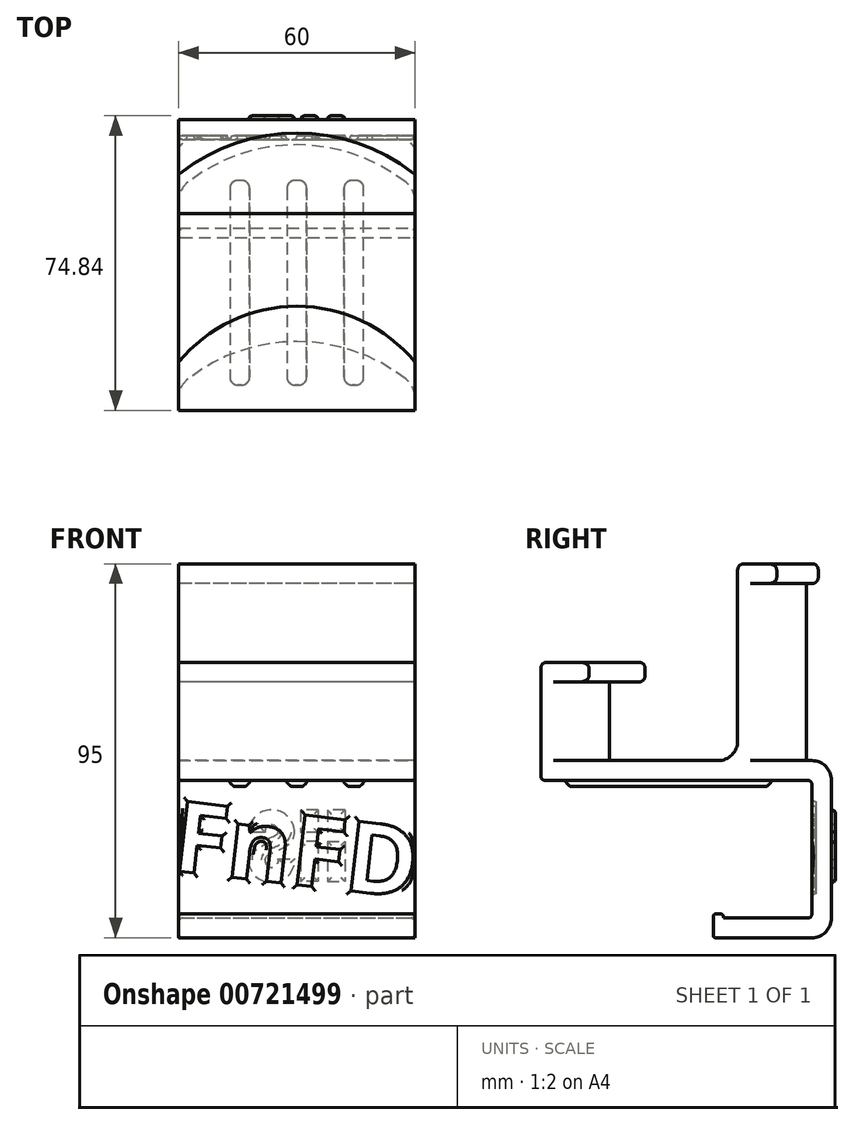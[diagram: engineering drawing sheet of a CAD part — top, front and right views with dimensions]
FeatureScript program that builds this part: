
annotation { "Feature Type Name" : "Feature", "Feature Type Description" : "" }
export const myFeature = defineFeature(function(context is Context, id is Id, definition is map)
    precondition{}
    {
        {
            var Q0;
            Q0=qCreatedBy(makeId("Top.planeOp"),FACE);
            var sketch = newSketch(context, id + "F0", { "sketchPlane" : qUnion([Q0])});
            skArc(sketch, "E0", {"start": v(27.7, 1.93) * mm, "mid": v(0, 11.46) * mm, "end": v(-27.7, 1.93) * mm});
            skLineSegment(sketch, "E1", {"start": v(0, 0) * mm, "end": v(0, -33.54) * mm, "construction": true});
            skLineSegment(sketch, "E2.bottom", {"start": v(-30, 0) * mm, "end": v(30, 0) * mm, "construction": true});
            skLineSegment(sketch, "E2.top", {"start": v(-30, -6) * mm, "end": v(30, -6) * mm});
            skLineSegment(sketch, "E2.left", {"start": v(-30, -2.8) * mm, "end": v(-30, -6) * mm});
            skLineSegment(sketch, "E2.right", {"start": v(30, -2.8) * mm, "end": v(30, -6) * mm});
            skPoint(sketch, "E3.visualSharp", {"position": v(30, 0) * mm});
            skArc(sketch, "E3.filletArc", {"start": v(30, -2.8) * mm, "mid": v(29.4, -0.17) * mm, "end": v(27.7, 1.93) * mm});
            skPoint(sketch, "E4.visualSharp", {"position": v(-30, 0) * mm});
            skArc(sketch, "E4.filletArc", {"start": v(-27.7, 1.93) * mm, "mid": v(-29.4, -0.17) * mm, "end": v(-30, -2.8) * mm});
            skSolve(sketch);
        }
        {
            var Q0;
            Q0=makeQuery(id+"F0.imprint","IMPRINT",FACE,{"disambiguationData":[TD([[makeQuery(id+"F0.imprint","IMPRINT",EDGE,{"derivedFrom":sQuery(id+"F0.wireOp",EDGE,"E0")}),1.0]])]});
            extrude(context, id + "F1", {"entities" : qUnion([Q0]), "depth" : 45 * mm, "offsetDistance" : 25 * mm});
        }
        {
            var Q0;
            Q0=makeQuery(id+"F1.opExtrude","CAP_FACE",FACE,{"disambiguationData":[OSD([sQuery(id+"F0.wireOp",EDGE,"E0"),sQuery(id+"F0.wireOp",EDGE,"E2.top"),sQuery(id+"F0.wireOp",EDGE,"E2.left"),sQuery(id+"F0.wireOp",EDGE,"E2.right"),sQuery(id+"F0.wireOp",EDGE,"E3.filletArc"),sQuery(id+"F0.wireOp",EDGE,"E4.filletArc")])],"isStart":false});
            var sketch = newSketch(context, id + "F2", { "sketchPlane" : qUnion([Q0])});
            skArc(sketch, "E5.0", {"start": v(33, -2.8) * mm, "mid": v(32.09, 1.15) * mm, "end": v(29.54, 4.3) * mm});
            skArc(sketch, "E5.1", {"start": v(-29.54, 4.3) * mm, "mid": v(-32.09, 1.15) * mm, "end": v(-33, -2.8) * mm});
            skLineSegment(sketch, "E5.2", {"start": v(-33, -2.8) * mm, "end": v(-33, -9) * mm});
            skArc(sketch, "E5.3", {"start": v(29.54, 4.3) * mm, "mid": v(0, 14.46) * mm, "end": v(-29.54, 4.3) * mm});
            skLineSegment(sketch, "E5.4", {"start": v(-33, -9) * mm, "end": v(33, -9) * mm});
            skLineSegment(sketch, "E5.5", {"start": v(33, -2.8) * mm, "end": v(33, -9) * mm});
            skLineSegment(sketch, "E6", {"start": v(-30, -6) * mm, "end": v(-33, -6) * mm});
            skPoint(sketch, "E6.endSnap0", {"position": v(-33, -5.9) * mm});
            skLineSegment(sketch, "E7", {"start": v(30, -6) * mm, "end": v(33, -6) * mm});
            skPoint(sketch, "E7.endSnap0", {"position": v(33, -5.9) * mm});
            skSolve(sketch);
        }
        {
            var Q0;
            Q0=makeQuery(id+"F2.imprint","IMPRINT",FACE,{"disambiguationData":[TD([[makeQuery(id+"F2.imprint","IMPRINT",EDGE,{"derivedFrom":sQuery(id+"F2.wireOp",EDGE,"E5.0")}),1.0]])]});
            var Q1;
            Q1=makeQuery(id+"F2.imprint","IMPRINT",FACE,{"disambiguationData":[TD([[makeQuery(id+"F2.imprint","IMPRINT",EDGE,{"derivedFrom":makeQuery(id+"F1.opExtrude","CAP_EDGE",EDGE,{"disambiguationData":[OSD([sQuery(id+"F0.wireOp",EDGE,"E0")])],"isStart":false})}),1.0]])]});
            extrude(context, id + "F3", {"entities" : qUnion([Q0, Q1]), "operationType" : NewBodyOperationType.ADD, "depth" : 5 * mm, "offsetDistance" : 25 * mm});
        }
        {
            var Q0;
            Q0=makeQuery(id+"F1.opExtrude","CAP_EDGE",EDGE,{"disambiguationData":[OSD([sQuery(id+"F0.wireOp",EDGE,"E0")])],"isStart":false});
            var Q1;
            Q1=makeQuery(id+"F3.opExtrude","CAP_EDGE",EDGE,{"disambiguationData":[OSD([sQuery(id+"F2.wireOp",EDGE,"E5.3")])],"isStart":true});
            var Q2;
            Q2=makeQuery(id+"F3.opExtrude","CAP_EDGE",EDGE,{"disambiguationData":[OSD([sQuery(id+"F2.wireOp",EDGE,"E5.3")])],"isStart":false});
            var Q3;
            Q3=makeQuery(id+"F1.opExtrude","CAP_EDGE",EDGE,{"disambiguationData":[OSD([sQuery(id+"F0.wireOp",EDGE,"E4.filletArc")])],"isStart":false});
            var Q4;
            Q4=makeQuery(id+"F3.opExtrude","CAP_EDGE",EDGE,{"disambiguationData":[OSD([sQuery(id+"F2.wireOp",EDGE,"E5.1")])],"isStart":true});
            var Q5;
            Q5=makeQuery(id+"F1.opExtrude","CAP_EDGE",EDGE,{"disambiguationData":[OSD([sQuery(id+"F0.wireOp",EDGE,"E2.left")])],"isStart":false});
            var Q6;
            Q6=makeQuery(id+"F3.opExtrude","CAP_EDGE",EDGE,{"disambiguationData":[OSD([sQuery(id+"F2.wireOp",EDGE,"E5.2")])],"isStart":true});
            var Q7;
            Q7=makeQuery(id+"F3.opExtrude","CAP_EDGE",EDGE,{"disambiguationData":[OSD([sQuery(id+"F2.wireOp",EDGE,"E5.1")])],"isStart":false});
            var Q8;
            Q8=makeQuery(id+"F3.opExtrude","CAP_EDGE",EDGE,{"disambiguationData":[OSD([sQuery(id+"F2.wireOp",EDGE,"E5.2")])],"isStart":false});
            var Q9;
            Q9=makeQuery(id+"F3.opExtrude","CAP_EDGE",EDGE,{"disambiguationData":[OSD([sQuery(id+"F2.wireOp",EDGE,"E5.0")])],"isStart":true});
            var Q10;
            Q10=makeQuery(id+"F3.opExtrude","CAP_EDGE",EDGE,{"disambiguationData":[OSD([sQuery(id+"F2.wireOp",EDGE,"E5.0")])],"isStart":false});
            var Q11;
            Q11=makeQuery(id+"F3.opExtrude","CAP_EDGE",EDGE,{"disambiguationData":[OSD([sQuery(id+"F2.wireOp",EDGE,"E5.5")])],"isStart":true});
            var Q12;
            Q12=makeQuery(id+"F3.opExtrude","CAP_EDGE",EDGE,{"disambiguationData":[OSD([sQuery(id+"F2.wireOp",EDGE,"E5.5")])],"isStart":false});
            var Q13;
            Q13=makeQuery(id+"F1.opExtrude","CAP_EDGE",EDGE,{"disambiguationData":[OSD([sQuery(id+"F0.wireOp",EDGE,"E3.filletArc")])],"isStart":false});
            var Q14;
            Q14=makeQuery(id+"F1.opExtrude","CAP_EDGE",EDGE,{"disambiguationData":[OSD([sQuery(id+"F0.wireOp",EDGE,"E2.right")])],"isStart":false});
            fillet(context, id + "F4", {"entities" : qUnion([Q0, Q1, Q2, Q3, Q4, Q5, Q6, Q7, Q8, Q9, Q10, Q11, Q12, Q13, Q14]), "radius" : 1.5 * mm, "tangentPropagation" : true, "allowEdgeOverflow" : false});
        }
        {
            var Q0;
            Q0=makeQuery(id+"F1.opExtrude","CAP_FACE",FACE,{"disambiguationData":[OSD([sQuery(id+"F0.wireOp",EDGE,"E0"),sQuery(id+"F0.wireOp",EDGE,"E2.top"),sQuery(id+"F0.wireOp",EDGE,"E2.left"),sQuery(id+"F0.wireOp",EDGE,"E2.right"),sQuery(id+"F0.wireOp",EDGE,"E3.filletArc"),sQuery(id+"F0.wireOp",EDGE,"E4.filletArc")])],"isStart":true});
            var sketch = newSketch(context, id + "F5", { "sketchPlane" : qUnion([Q0])});
            skLineSegment(sketch, "E8.bottom", {"start": v(-30, 6) * mm, "end": v(30, 6) * mm});
            skLineSegment(sketch, "E8.top", {"start": v(-30, -17.84) * mm, "end": v(30, -17.84) * mm});
            skLineSegment(sketch, "E8.left", {"start": v(-30, 6) * mm, "end": v(-30, -17.84) * mm});
            skLineSegment(sketch, "E8.right", {"start": v(30, 6) * mm, "end": v(30, -17.84) * mm});
            skLineSegment(sketch, "E9.bottom", {"start": v(-30, 6) * mm, "end": v(30, 6) * mm, "construction": true});
            skLineSegment(sketch, "E9.top", {"start": v(-30, 56) * mm, "end": v(30, 56) * mm});
            skLineSegment(sketch, "E9.left", {"start": v(-30, 6) * mm, "end": v(-30, 56) * mm});
            skLineSegment(sketch, "E9.right", {"start": v(30, 6) * mm, "end": v(30, 56) * mm});
            skSolve(sketch);
        }
        {
            var Q0;
            {var subQ2=sQuery(id+"F5.wireOp",EDGE,"E8.top");Q0=makeQuery(id+"F5.imprint","IMPRINT",FACE,{"disambiguationData":[TD([[makeQuery(id+"F5.imprint","IMPRINT",EDGE,{"derivedFrom":subQ2}),1.0]])]});}
            var Q1;
            {var subQ1=sQuery(id+"F5.wireOp",EDGE,"E8.bottom");Q1=makeQuery(id+"F5.imprint","IMPRINT",FACE,{"disambiguationData":[TD([[makeQuery(id+"F5.imprint","IMPRINT",EDGE,{"derivedFrom":subQ1}),-1.0]])]});}
            var Q2;
            Q2=makeQuery(id+"F5.imprint","IMPRINT",FACE,{"disambiguationData":[TD([[makeQuery(id+"F5.imprint","IMPRINT",EDGE,{"derivedFrom":sQuery(id+"F5.wireOp",EDGE,"E8.bottom")}),1.0]])]});
            extrude(context, id + "F6", {"entities" : qUnion([Q0, Q1, Q2]), "operationType" : NewBodyOperationType.ADD, "depth" : 5 * mm, "offsetDistance" : 25 * mm});
        }
        {
            var Q0;
            Q0=makeQuery(id+"F6.opExtrude","CAP_FACE",FACE,{"disambiguationData":[OSD([sQuery(id+"F5.wireOp",EDGE,"E8.top"),sQuery(id+"F5.wireOp",EDGE,"E8.left"),sQuery(id+"F5.wireOp",EDGE,"E8.right"),sQuery(id+"F5.wireOp",EDGE,"E9.top"),sQuery(id+"F5.wireOp",EDGE,"E9.left"),sQuery(id+"F5.wireOp",EDGE,"E9.right")])],"isStart":false});
            var sketch = newSketch(context, id + "F7", { "sketchPlane" : qUnion([Q0])});
            skLineSegment(sketch, "E10.bottom", {"start": v(-30, -17.84) * mm, "end": v(30, -17.84) * mm});
            skLineSegment(sketch, "E10.top", {"start": v(-30, -12.84) * mm, "end": v(30, -12.84) * mm});
            skLineSegment(sketch, "E10.left", {"start": v(-30, -17.84) * mm, "end": v(-30, -12.84) * mm});
            skLineSegment(sketch, "E10.right", {"start": v(30, -17.84) * mm, "end": v(30, -12.84) * mm});
            skSolve(sketch);
        }
        {
            var Q0;
            Q0=makeQuery(id+"F7.imprint","IMPRINT",FACE,{"disambiguationData":[TD([[makeQuery(id+"F7.imprint","IMPRINT",EDGE,{"derivedFrom":sQuery(id+"F7.wireOp",EDGE,"E10.bottom")}),1.0]])]});
            extrude(context, id + "F8", {"entities" : qUnion([Q0]), "operationType" : NewBodyOperationType.ADD, "depth" : 35 * mm, "offsetDistance" : 25 * mm});
        }
        {
            var Q0;
            Q0=makeQuery(id+"F8.opExtrude","CAP_FACE",FACE,{"disambiguationData":[OSD([sQuery(id+"F7.wireOp",EDGE,"E10.bottom"),sQuery(id+"F7.wireOp",EDGE,"E10.top"),sQuery(id+"F7.wireOp",EDGE,"E10.left"),sQuery(id+"F7.wireOp",EDGE,"E10.right")])],"isStart":false});
            var sketch = newSketch(context, id + "F9", { "sketchPlane" : qUnion([Q0])});
            skLineSegment(sketch, "E11.bottom", {"start": v(-30, -17.84) * mm, "end": v(30, -17.84) * mm});
            skLineSegment(sketch, "E11.top", {"start": v(-30, 12.16) * mm, "end": v(30, 12.16) * mm});
            skLineSegment(sketch, "E11.left", {"start": v(-30, -17.84) * mm, "end": v(-30, 12.16) * mm});
            skLineSegment(sketch, "E11.right", {"start": v(30, -17.84) * mm, "end": v(30, 12.16) * mm});
            skSolve(sketch);
        }
        {
            var Q0;
            {var subQ0=sQuery(id+"F9.wireOp",EDGE,"E11.top");Q0=makeQuery(id+"F9.imprint","IMPRINT",FACE,{"disambiguationData":[TD([[makeQuery(id+"F9.imprint","IMPRINT",EDGE,{"derivedFrom":subQ0}),-1.0]])]});}
            var Q1;
            {var subQ0=sQuery(id+"F9.wireOp",EDGE,"E11.bottom");Q1=makeQuery(id+"F9.imprint","IMPRINT",FACE,{"disambiguationData":[TD([[makeQuery(id+"F9.imprint","IMPRINT",EDGE,{"derivedFrom":subQ0}),1.0]])]});}
            extrude(context, id + "F10", {"entities" : qUnion([Q0, Q1]), "operationType" : NewBodyOperationType.ADD, "depth" : 5 * mm, "offsetDistance" : 25 * mm});
        }
        {
            var Q0;
            Q0=makeQuery(id+"F10.opExtrude","CAP_FACE",FACE,{"disambiguationData":[OSD([sQuery(id+"F9.wireOp",EDGE,"E11.bottom"),sQuery(id+"F9.wireOp",EDGE,"E11.top"),sQuery(id+"F9.wireOp",EDGE,"E11.left"),sQuery(id+"F9.wireOp",EDGE,"E11.right")])],"isStart":true});
            var sketch = newSketch(context, id + "F11", { "sketchPlane" : qUnion([Q0])});
            skLineSegment(sketch, "E12.bottom", {"start": v(-30, -12.16) * mm, "end": v(30, -12.16) * mm});
            skLineSegment(sketch, "E12.top", {"start": v(-30, -9.66) * mm, "end": v(30, -9.66) * mm});
            skLineSegment(sketch, "E12.left", {"start": v(-30, -12.16) * mm, "end": v(-30, -9.66) * mm});
            skLineSegment(sketch, "E12.right", {"start": v(30, -12.16) * mm, "end": v(30, -9.66) * mm});
            skSolve(sketch);
        }
        {
            var Q0;
            Q0=makeQuery(id+"F11.imprint","IMPRINT",FACE,{"disambiguationData":[TD([[makeQuery(id+"F11.imprint","IMPRINT",EDGE,{"derivedFrom":sQuery(id+"F11.wireOp",EDGE,"E12.bottom")}),1.0]])]});
            extrude(context, id + "F12", {"entities" : qUnion([Q0]), "operationType" : NewBodyOperationType.ADD, "depth" : 1 * mm, "offsetDistance" : 25 * mm});
        }
        {
            var Q0;
            Q0=makeQuery(id+"F8.opExtrude","CAP_EDGE",EDGE,{"disambiguationData":[OSD([sQuery(id+"F7.wireOp",EDGE,"E10.top")])],"isStart":true});
            var Q1;
            Q1=makeQuery(id+"F8.opExtrude","CAP_EDGE",EDGE,{"disambiguationData":[OSD([sQuery(id+"F7.wireOp",EDGE,"E10.top")])],"isStart":false});
            var Q2;
            Q2=makeQuery(id+"F1.opExtrude","CAP_EDGE",EDGE,{"disambiguationData":[OSD([sQuery(id+"F0.wireOp",EDGE,"E2.top")])],"isStart":true});
            var Q3;
            Q3=makeQuery(id+"F6.opExtrude","CAP_EDGE",EDGE,{"disambiguationData":[OSD([sQuery(id+"F5.wireOp",EDGE,"E8.top")])],"isStart":true});
            var Q4;
            Q4=makeQuery(id+"F10.opExtrude","CAP_EDGE",EDGE,{"disambiguationData":[OSD([sQuery(id+"F9.wireOp",EDGE,"E11.bottom")])],"isStart":false});
            fillet(context, id + "F13", {"entities" : qUnion([Q0, Q1, Q2, Q3, Q4]), "radius" : 5 * mm, "tangentPropagation" : true, "allowEdgeOverflow" : false});
        }
        {
            var Q0;
            Q0=makeQuery(id+"F8.opExtrude","SWEPT_FACE",FACE,{"disambiguationData":[OSD([sQuery(id+"F7.wireOp",EDGE,"E10.top")])]});
            var sketch = newSketch(context, id + "F14", { "sketchPlane" : qUnion([Q0])});
            skText(sketch, "E13", { "text": "FnFD", "fontName": "OpenSans-Bold.ttf"});
            const initialGuessF14  = {"E13": [-0.03206, -0.02786, 0.99344, -0.11434, 0.01798]};
            skSetInitialGuess(sketch, initialGuessF14);
            skSolve(sketch);
        }
        {
            var Q0;
            Q0=makeQuery(id+"F14.imprint","IMPRINT",FACE,{"disambiguationData":[TD([[makeQuery(id+"F14.imprint","IMPRINT",EDGE,{"derivedFrom":sQuery(id+"F14.wireOp",EDGE,"E13.sketch_text.stroke-0")}),-1.0]])]});
            var Q1;
            Q1=makeQuery(id+"F14.imprint","IMPRINT",FACE,{"disambiguationData":[TD([[makeQuery(id+"F14.imprint","IMPRINT",EDGE,{"derivedFrom":sQuery(id+"F14.wireOp",EDGE,"E13.sketch_text.stroke-10")}),-1.0]])]});
            var Q2;
            Q2=makeQuery(id+"F14.imprint","IMPRINT",FACE,{"disambiguationData":[TD([[makeQuery(id+"F14.imprint","IMPRINT",EDGE,{"derivedFrom":sQuery(id+"F14.wireOp",EDGE,"E13.sketch_text.stroke-27")}),-1.0]])]});
            var Q3;
            Q3=makeQuery(id+"F14.imprint","IMPRINT",FACE,{"disambiguationData":[TD([[makeQuery(id+"F14.imprint","IMPRINT",EDGE,{"derivedFrom":sQuery(id+"F14.wireOp",EDGE,"E13.sketch_text.stroke-37")}),-1.0]])]});
            var Q4;
            {var subQ6=sQuery(id+"F14.wireOp",EDGE,"E13.sketch_text.stroke-2");Q4=makeQuery(id+"F14.imprint","IMPRINT",FACE,{"disambiguationData":[TD([[makeQuery(id+"F14.imprint","IMPRINT",EDGE,{"derivedFrom":subQ6}),-1.0]])]});}
            extrude(context, id + "F15", {"entities" : qUnion([Q0, Q1, Q2, Q3, Q4]), "operationType" : NewBodyOperationType.REMOVE, "oppositeDirection" : true, "depth" : 1 * mm, "offsetDistance" : 25 * mm});
        }
        {
            var Q0;
            {var subQ0=sQuery(id+"F0.wireOp",EDGE,"E2.top");var subQ1=sQuery(id+"F5.wireOp",EDGE,"E9.top");var subQ2=sQuery(id+"F5.wireOp",EDGE,"E9.right");var subQ3=sQuery(id+"F5.wireOp",EDGE,"E8.right");var subQ4=sQuery(id+"F5.wireOp",EDGE,"E9.left");var subQ5=sQuery(id+"F5.wireOp",EDGE,"E8.left");Q0=makeQuery(id+"F6.boolean.opBoolean","SPLIT",FACE,{"disambiguationData":[TD([makeQuery(id+"F1.opExtrude","SWEPT_FACE",FACE,{"disambiguationData":[OSD([subQ0])]})])],"derivedFrom":makeQuery(id+"F6.opExtrude","CAP_FACE",FACE,{"disambiguationData":[OSD([sQuery(id+"F5.wireOp",EDGE,"E8.top"),subQ5,subQ3,subQ1,subQ4,subQ2])],"isStart":true})});}
            var sketch = newSketch(context, id + "F16", { "sketchPlane" : qUnion([Q0])});
            skArc(sketch, "E14", {"start": v(27.7, -48.07) * mm, "mid": v(0, -38.54) * mm, "end": v(-27.7, -48.07) * mm});
            skLineSegment(sketch, "E15", {"start": v(0, -38.54) * mm, "end": v(0, -83.54) * mm, "construction": true});
            skLineSegment(sketch, "E16.bottom", {"start": v(-30, -50) * mm, "end": v(30, -50) * mm, "construction": true});
            skLineSegment(sketch, "E16.top", {"start": v(-30, -56) * mm, "end": v(30, -56) * mm});
            skLineSegment(sketch, "E16.left", {"start": v(-30, -52.8) * mm, "end": v(-30, -56) * mm});
            skLineSegment(sketch, "E16.right", {"start": v(30, -52.8) * mm, "end": v(30, -56) * mm});
            skPoint(sketch, "E17.visualSharp", {"position": v(30, -50) * mm});
            skArc(sketch, "E17.filletArc", {"start": v(30, -52.8) * mm, "mid": v(29.4, -50.17) * mm, "end": v(27.7, -48.07) * mm});
            skPoint(sketch, "E18.visualSharp", {"position": v(-30, -50) * mm});
            skArc(sketch, "E18.filletArc", {"start": v(-27.7, -48.07) * mm, "mid": v(-29.4, -50.17) * mm, "end": v(-30, -52.8) * mm});
            skSolve(sketch);
        }
        {
            var Q0;
            Q0=makeQuery(id+"F16.imprint","IMPRINT",FACE,{"disambiguationData":[TD([[makeQuery(id+"F16.imprint","IMPRINT",EDGE,{"derivedFrom":sQuery(id+"F16.wireOp",EDGE,"E14")}),1.0]])]});
            extrude(context, id + "F17", {"entities" : qUnion([Q0]), "operationType" : NewBodyOperationType.ADD, "depth" : 20 * mm, "offsetDistance" : 25 * mm});
        }
        {
            var Q0;
            Q0=makeQuery(id+"F17.opExtrude","CAP_FACE",FACE,{"disambiguationData":[OSD([sQuery(id+"F16.wireOp",EDGE,"E14"),sQuery(id+"F16.wireOp",EDGE,"E16.top"),sQuery(id+"F16.wireOp",EDGE,"E16.left"),sQuery(id+"F16.wireOp",EDGE,"E16.right"),sQuery(id+"F16.wireOp",EDGE,"E17.filletArc"),sQuery(id+"F16.wireOp",EDGE,"E18.filletArc")])],"isStart":false});
            var sketch = newSketch(context, id + "F18", { "sketchPlane" : qUnion([Q0])});
            skLineSegment(sketch, "E19.2", {"start": v(-33, -48) * mm, "end": v(-33, -56) * mm});
            skLineSegment(sketch, "E19.4", {"start": v(-33, -56) * mm, "end": v(33, -56) * mm});
            skLineSegment(sketch, "E19.5", {"start": v(33, -48) * mm, "end": v(33, -56) * mm});
            skLineSegment(sketch, "E20", {"start": v(-30, -53) * mm, "end": v(-33, -53) * mm});
            skPoint(sketch, "E20.endSnap0", {"position": v(-33, -52) * mm});
            skLineSegment(sketch, "E21", {"start": v(30, -52.56) * mm, "end": v(33, -52.56) * mm});
            skPoint(sketch, "E21.endSnap0", {"position": v(33, -52) * mm});
            skLineSegment(sketch, "E22", {"start": v(0, -56) * mm, "end": v(0, -52.75) * mm, "construction": true});
            skLineSegment(sketch, "E23", {"start": v(0, -56) * mm, "end": v(0, -60.11) * mm, "construction": true});
            skArc(sketch, "E24", {"start": v(33, -48) * mm, "mid": v(0, -29.54) * mm, "end": v(-33, -48) * mm});
            skSolve(sketch);
        }
        {
            var Q0;
            {var subQ3=sQuery(id+"F18.wireOp",EDGE,"E19.0");Q0=makeQuery(id+"F18.imprint","IMPRINT",FACE,{"disambiguationData":[TD([[makeQuery(id+"F18.imprint","IMPRINT",EDGE,{"derivedFrom":subQ3}),1.0]])]});}
            var Q1;
            Q1=makeQuery(id+"F18.imprint","IMPRINT",FACE,{"disambiguationData":[TD([[makeQuery(id+"F18.imprint","IMPRINT",EDGE,{"derivedFrom":makeQuery(id+"F17.opExtrude","CAP_EDGE",EDGE,{"disambiguationData":[OSD([sQuery(id+"F16.wireOp",EDGE,"E14")])],"isStart":false})}),1.0]])]});
            var Q2;
            {var subQ3=sQuery(id+"F18.wireOp",EDGE,"E20");Q2=makeQuery(id+"F18.imprint","IMPRINT",FACE,{"disambiguationData":[TD([[makeQuery(id+"F18.imprint","IMPRINT",EDGE,{"derivedFrom":subQ3}),1.0]])]});}
            var Q3;
            {var subQ5=sQuery(id+"F18.wireOp",EDGE,"E21");Q3=makeQuery(id+"F18.imprint","IMPRINT",FACE,{"disambiguationData":[TD([[makeQuery(id+"F18.imprint","IMPRINT",EDGE,{"derivedFrom":subQ5}),-1.0]])]});}
            var Q4;
            {var subQ3=sQuery(id+"F18.wireOp",EDGE,"E20");Q4=makeQuery(id+"F18.imprint","IMPRINT",FACE,{"disambiguationData":[TD([[makeQuery(id+"F18.imprint","IMPRINT",EDGE,{"derivedFrom":subQ3}),-1.0]])]});}
            extrude(context, id + "F19", {"entities" : qUnion([Q0, Q1, Q2, Q3, Q4]), "operationType" : NewBodyOperationType.ADD, "depth" : 5 * mm, "offsetDistance" : 25 * mm});
        }
        {
            var Q0;
            Q0=makeQuery(id+"F17.opExtrude","CAP_EDGE",EDGE,{"disambiguationData":[OSD([sQuery(id+"F16.wireOp",EDGE,"E14")])],"isStart":true});
            var Q1;
            Q1=makeQuery(id+"F19.opExtrude","CAP_EDGE",EDGE,{"disambiguationData":[OSD([sQuery(id+"F18.wireOp",EDGE,"E19.3")])],"isStart":false});
            var Q2;
            Q2=makeQuery(id+"F19.opExtrude","CAP_EDGE",EDGE,{"disambiguationData":[OSD([sQuery(id+"F18.wireOp",EDGE,"E19.3")])],"isStart":true});
            var Q3;
            Q3=makeQuery(id+"F1.opExtrude","CAP_EDGE",EDGE,{"disambiguationData":[OSD([sQuery(id+"F0.wireOp",EDGE,"E0")])],"isStart":true});
            var Q4;
            Q4=makeQuery(id+"F17.opExtrude","CAP_EDGE",EDGE,{"disambiguationData":[OSD([sQuery(id+"F16.wireOp",EDGE,"E14")])],"isStart":false});
            var Q5;
            Q5=makeQuery(id+"F3.opExtrude","CAP_EDGE",EDGE,{"disambiguationData":[OSD([sQuery(id+"F0.wireOp",EDGE,"E2.top"),sQuery(id+"F2.wireOp",EDGE,"E6"),sQuery(id+"F2.wireOp",EDGE,"E7")])],"isStart":false});
            var Q6;
            Q6=makeQuery(id+"F19.opExtrude","CAP_EDGE",EDGE,{"disambiguationData":[OSD([sQuery(id+"F18.wireOp",EDGE,"E19.4")])],"isStart":false});
            var Q7;
            Q7=makeQuery(id+"F19.opExtrude","CAP_EDGE",EDGE,{"disambiguationData":[OSD([sQuery(id+"F18.wireOp",EDGE,"E24")])],"isStart":true});
            var Q8;
            Q8=makeQuery(id+"F19.opExtrude","CAP_EDGE",EDGE,{"disambiguationData":[OSD([sQuery(id+"F18.wireOp",EDGE,"E24")])],"isStart":false});
            fillet(context, id + "F20", {"entities" : qUnion([Q0, Q1, Q2, Q3, Q4, Q5, Q6, Q7, Q8]), "radius" : 1.5 * mm, "tangentPropagation" : true, "allowEdgeOverflow" : false});
        }
        {
            var Q0;
            {var subQ0=sQuery(id+"F7.wireOp",EDGE,"E10.top");Q0=makeQuery(id+"F15.boolean.opBoolean","SPLIT",FACE,{"disambiguationData":[TD([makeQuery(id+"F1.opExtrude","SWEPT_FACE",FACE,{"disambiguationData":[OSD([sQuery(id+"F0.wireOp",EDGE,"E2.left")])]})])],"derivedFrom":makeQuery(id+"F8.opExtrude","SWEPT_FACE",FACE,{"disambiguationData":[OSD([subQ0])]})});}
            var Q1;
            Q1=makeQuery(id+"F6.opExtrude","CAP_EDGE",EDGE,{"disambiguationData":[OSD([sQuery(id+"F5.wireOp",EDGE,"E9.top")])],"isStart":true});
            var Q2;
            Q2=makeQuery(id+"F6.opExtrude","CAP_EDGE",EDGE,{"disambiguationData":[OSD([sQuery(id+"F5.wireOp",EDGE,"E9.top")])],"isStart":false});
            fillet(context, id + "F21", {"entities" : qUnion([Q0, Q1, Q2]), "radius" : 1 * mm, "tangentPropagation" : true, "allowEdgeOverflow" : false});
        }
        {
            var Q0;
            Q0=makeQuery(id+"F10.opExtrude","CAP_FACE",FACE,{"disambiguationData":[OSD([sQuery(id+"F9.wireOp",EDGE,"E11.bottom"),sQuery(id+"F9.wireOp",EDGE,"E11.top"),sQuery(id+"F9.wireOp",EDGE,"E11.left"),sQuery(id+"F9.wireOp",EDGE,"E11.right")])],"isStart":false});
            var sketch = newSketch(context, id + "F22", { "sketchPlane" : qUnion([Q0])});
            skLineSegment(sketch, "E25.top", {"start": v(-30, -18.33) * mm, "end": v(30, -18.33) * mm});
            skLineSegment(sketch, "E25.left", {"start": v(-30, 12.16) * mm, "end": v(-30, -18.33) * mm});
            skLineSegment(sketch, "E25.right", {"start": v(30, 31.6) * mm, "end": v(30, -18.33) * mm});
            skLineSegment(sketch, "E26.0", {"start": v(-35, 87.47) * mm, "end": v(-35, -23.33) * mm});
            skLineSegment(sketch, "E26.1", {"start": v(-35, 87.47) * mm, "end": v(35, 87.47) * mm});
            skLineSegment(sketch, "E26.2", {"start": v(35, 87.47) * mm, "end": v(35, -23.33) * mm});
            skLineSegment(sketch, "E26.3", {"start": v(-35, -23.33) * mm, "end": v(35, -23.33) * mm});
            skLineSegment(sketch, "E27", {"start": v(-30, 12.16) * mm, "end": v(-30, 60.9) * mm});
            skLineSegment(sketch, "E28", {"start": v(-30, 60.9) * mm, "end": v(30, 60.9) * mm});
            skLineSegment(sketch, "E29", {"start": v(30, 60.9) * mm, "end": v(30, 31.6) * mm});
            skSolve(sketch);
        }
        {
            var Q0;
            Q0=makeQuery(id+"F22.imprint","IMPRINT",FACE,{"disambiguationData":[TD([[makeQuery(id+"F22.imprint","IMPRINT",EDGE,{"derivedFrom":sQuery(id+"F22.wireOp",EDGE,"E27")}),-1.0]])]});
            var Q1;
            {var subQ1=sQuery(id+"F9.wireOp",EDGE,"E11.top");var subQ2=makeQuery(id+"F10.opExtrude","CAP_EDGE",EDGE,{"disambiguationData":[OSD([subQ1])],"isStart":false});Q1=makeQuery(id+"F22.imprint","IMPRINT",FACE,{"disambiguationData":[TD([[makeQuery(id+"F22.imprint","IMPRINT",EDGE,{"derivedFrom":subQ2}),-1.0]])]});}
            var Q2;
            {var subQ0=sQuery(id+"F22.wireOp",EDGE,"E25.top");Q2=makeQuery(id+"F22.imprint","IMPRINT",FACE,{"disambiguationData":[TD([[makeQuery(id+"F22.imprint","IMPRINT",EDGE,{"derivedFrom":subQ0}),1.0]])]});}
            extrude(context, id + "F23", {"entities" : qUnion([Q0, Q1, Q2]), "operationType" : NewBodyOperationType.INTERSECT, "oppositeDirection" : true, "depth" : 126.3 * mm, "offsetDistance" : 25 * mm});
        }
        {
            var Q0;
            Q0=makeQuery(id+"F10.boolean.opBoolean","MERGE",FACE,{"derivedFrom":[makeQuery(id+"F8.boolean.opBoolean","MERGE",FACE,{"derivedFrom":[makeQuery(id+"F6.opExtrude","SWEPT_FACE",FACE,{"disambiguationData":[OSD([sQuery(id+"F5.wireOp",EDGE,"E8.top")])]}),makeQuery(id+"F8.opExtrude","SWEPT_FACE",FACE,{"disambiguationData":[OSD([sQuery(id+"F7.wireOp",EDGE,"E10.bottom")])]})]}),makeQuery(id+"F10.opExtrude","SWEPT_FACE",FACE,{"disambiguationData":[OSD([sQuery(id+"F9.wireOp",EDGE,"E11.bottom")])]})]});
            var sketch = newSketch(context, id + "F24", { "sketchPlane" : qUnion([Q0])});
            skLineSegment(sketch, "E30.bottom", {"start": v(-12.2, -12.54) * mm, "end": v(-7.75, -12.54) * mm});
            skLineSegment(sketch, "E30.top", {"start": v(-12.2, -18.28) * mm, "end": v(-7.75, -18.28) * mm});
            skLineSegment(sketch, "E30.left", {"start": v(-12.2, -12.54) * mm, "end": v(-12.2, -18.28) * mm});
            skLineSegment(sketch, "E30.right", {"start": v(-7.75, -12.54) * mm, "end": v(-7.75, -18.28) * mm});
            skLineSegment(sketch, "E31.bottom", {"start": v(-7.78, -20.53) * mm, "end": v(-12.24, -20.53) * mm});
            skLineSegment(sketch, "E31.top", {"start": v(-7.78, -30.72) * mm, "end": v(-12.24, -30.72) * mm});
            skLineSegment(sketch, "E31.left", {"start": v(-7.78, -20.53) * mm, "end": v(-7.78, -30.72) * mm});
            skLineSegment(sketch, "E31.right", {"start": v(-12.24, -20.53) * mm, "end": v(-12.24, -30.72) * mm});
            skLineSegment(sketch, "E32.bottom", {"start": v(-5.44, -12.54) * mm, "end": v(-0.98, -12.54) * mm});
            skLineSegment(sketch, "E32.top", {"start": v(-5.44, -18.28) * mm, "end": v(-0.98, -18.28) * mm});
            skLineSegment(sketch, "E32.left", {"start": v(-5.44, -12.54) * mm, "end": v(-5.44, -18.28) * mm});
            skLineSegment(sketch, "E32.right", {"start": v(-0.98, -12.54) * mm, "end": v(-0.98, -18.28) * mm});
            skLineSegment(sketch, "E33.bottom", {"start": v(-5.44, -20.53) * mm, "end": v(-0.98, -20.53) * mm});
            skLineSegment(sketch, "E33.top", {"start": v(-5.44, -30.72) * mm, "end": v(-0.98, -30.72) * mm});
            skLineSegment(sketch, "E33.left", {"start": v(-5.44, -20.53) * mm, "end": v(-5.44, -30.72) * mm});
            skLineSegment(sketch, "E33.right", {"start": v(-0.98, -20.53) * mm, "end": v(-0.98, -30.72) * mm});
            skArc(sketch, "E34", {"start": v(12.28, -18.23) * mm, "mid": v(6.4, -12.5) * mm, "end": v(0.54, -18.23) * mm});
            skArc(sketch, "E35", {"start": v(0.54, -24.96) * mm, "mid": v(6.25, -30.98) * mm, "end": v(12.28, -25.27) * mm});
            skArc(sketch, "E36", {"start": v(8.05, -18.23) * mm, "mid": v(6.4, -16.37) * mm, "end": v(4.75, -18.23) * mm});
            skArc(sketch, "E37", {"start": v(4.75, -24.96) * mm, "mid": v(6.21, -27.11) * mm, "end": v(8.05, -25.27) * mm});
            skFitSpline(sketch, "E38", {"points": [v(8.05, -25.27) * mm, v(7.59, -24.2) * mm, v(6, -23.29) * mm, v(3.2, -22.02) * mm, v(1.42, -20.61) * mm, v(0.54, -18.23) * mm], "startDerivative": vector(-1.03, 10.2) * mm, "endDerivative": vector(0.23, 9.56) * mm});
            skFitSpline(sketch, "E39", {"points": [v(4.75, -18.23) * mm, v(5.4, -19.1) * mm, v(7.25, -19.8) * mm, v(8.96, -20.56) * mm, v(11.06, -21.9) * mm, v(12.01, -23.25) * mm, v(12.23, -24.39) * mm, v(12.28, -25.27) * mm], "startDerivative": vector(3.8, -8.54) * mm, "endDerivative": vector(-0.25, -8.28) * mm});
            skLineSegment(sketch, "E40", {"start": v(8.05, -18.23) * mm, "end": v(12.28, -18.23) * mm});
            skLineSegment(sketch, "E41", {"start": v(4.75, -24.96) * mm, "end": v(0.54, -24.96) * mm});
            skLineSegment(sketch, "E42.filletArc", {"start": v(0.54, -18.23) * mm, "end": v(0.54, -18.23) * mm});
            skSolve(sketch);
        }
        {
            var Q0;
            Q0=makeQuery(id+"F24.imprint","IMPRINT",FACE,{"disambiguationData":[TD([[makeQuery(id+"F24.imprint","IMPRINT",EDGE,{"derivedFrom":sQuery(id+"F24.wireOp",EDGE,"E30.bottom")}),-1.0]])]});
            var Q1;
            Q1=makeQuery(id+"F24.imprint","IMPRINT",FACE,{"disambiguationData":[TD([[makeQuery(id+"F24.imprint","IMPRINT",EDGE,{"derivedFrom":sQuery(id+"F24.wireOp",EDGE,"E32.bottom")}),-1.0]])]});
            var Q2;
            Q2=makeQuery(id+"F24.imprint","IMPRINT",FACE,{"disambiguationData":[TD([[makeQuery(id+"F24.imprint","IMPRINT",EDGE,{"derivedFrom":sQuery(id+"F24.wireOp",EDGE,"E31.bottom")}),1.0]])]});
            var Q3;
            Q3=makeQuery(id+"F24.imprint","IMPRINT",FACE,{"disambiguationData":[TD([[makeQuery(id+"F24.imprint","IMPRINT",EDGE,{"derivedFrom":sQuery(id+"F24.wireOp",EDGE,"E33.bottom")}),-1.0]])]});
            var Q4;
            Q4=makeQuery(id+"F24.imprint","IMPRINT",FACE,{"disambiguationData":[TD([[makeQuery(id+"F24.imprint","IMPRINT",EDGE,{"derivedFrom":sQuery(id+"F24.wireOp",EDGE,"E34")}),1.0]])]});
            extrude(context, id + "F25", {"entities" : qUnion([Q0, Q1, Q2, Q3, Q4]), "operationType" : NewBodyOperationType.ADD, "depth" : 1 * mm, "offsetDistance" : 25 * mm});
        }
        {
            var Q0;
            Q0=makeQuery(id+"F25.opExtrude","CAP_FACE",FACE,{"disambiguationData":[OSD([sQuery(id+"F24.wireOp",EDGE,"E32.bottom"),sQuery(id+"F24.wireOp",EDGE,"E32.top"),sQuery(id+"F24.wireOp",EDGE,"E32.left"),sQuery(id+"F24.wireOp",EDGE,"E32.right")])],"isStart":false});
            var Q1;
            Q1=makeQuery(id+"F25.opExtrude","CAP_FACE",FACE,{"disambiguationData":[OSD([sQuery(id+"F24.wireOp",EDGE,"E31.bottom"),sQuery(id+"F24.wireOp",EDGE,"E31.top"),sQuery(id+"F24.wireOp",EDGE,"E31.left"),sQuery(id+"F24.wireOp",EDGE,"E31.right")])],"isStart":false});
            var Q2;
            Q2=makeQuery(id+"F25.opExtrude","CAP_FACE",FACE,{"disambiguationData":[OSD([sQuery(id+"F24.wireOp",EDGE,"E33.bottom"),sQuery(id+"F24.wireOp",EDGE,"E33.top"),sQuery(id+"F24.wireOp",EDGE,"E33.left"),sQuery(id+"F24.wireOp",EDGE,"E33.right")])],"isStart":false});
            var Q3;
            Q3=makeQuery(id+"F25.opExtrude","CAP_EDGE",EDGE,{"disambiguationData":[OSD([sQuery(id+"F24.wireOp",EDGE,"E30.bottom")])],"isStart":false});
            var Q4;
            Q4=makeQuery(id+"F25.opExtrude","CAP_FACE",FACE,{"disambiguationData":[OSD([sQuery(id+"F24.wireOp",EDGE,"E30.bottom"),sQuery(id+"F24.wireOp",EDGE,"E30.top"),sQuery(id+"F24.wireOp",EDGE,"E30.left"),sQuery(id+"F24.wireOp",EDGE,"E30.right")])],"isStart":false});
            var Q5;
            Q5=makeQuery(id+"F25.opExtrude","CAP_FACE",FACE,{"disambiguationData":[OSD([sQuery(id+"F24.wireOp",EDGE,"E34"),sQuery(id+"F24.wireOp",EDGE,"E35"),sQuery(id+"F24.wireOp",EDGE,"E36"),sQuery(id+"F24.wireOp",EDGE,"E37"),sQuery(id+"F24.wireOp",EDGE,"E38"),sQuery(id+"F24.wireOp",EDGE,"E39"),sQuery(id+"F24.wireOp",EDGE,"E40"),sQuery(id+"F24.wireOp",EDGE,"E41")])],"isStart":false});
            fillet(context, id + "F26", {"entities" : qUnion([Q0, Q1, Q2, Q3, Q4, Q5]), "radius" : 1 * mm, "tangentPropagation" : true, "allowEdgeOverflow" : false});
        }
        {
            var Q0;
            Q0=makeQuery(id+"F6.opExtrude","CAP_FACE",FACE,{"disambiguationData":[OSD([sQuery(id+"F5.wireOp",EDGE,"E8.top"),sQuery(id+"F5.wireOp",EDGE,"E8.left"),sQuery(id+"F5.wireOp",EDGE,"E8.right"),sQuery(id+"F5.wireOp",EDGE,"E9.top"),sQuery(id+"F5.wireOp",EDGE,"E9.left"),sQuery(id+"F5.wireOp",EDGE,"E9.right")])],"isStart":false});
            var sketch = newSketch(context, id + "F27", { "sketchPlane" : qUnion([Q0])});
            skLineSegment(sketch, "E43", {"start": v(0, 55) * mm, "end": v(0, -7.84) * mm, "construction": true});
            skLineSegment(sketch, "E44", {"start": v(29, 23.58) * mm, "end": v(0, 23.58) * mm, "construction": true});
            skLineSegment(sketch, "E45", {"start": v(-29, 23.58) * mm, "end": v(0, 23.58) * mm, "construction": true});
            skLineSegment(sketch, "E46.bottom", {"start": v(15, 49.58) * mm, "end": v(14, 49.58) * mm});
            skLineSegment(sketch, "E46.top", {"start": v(15, -2.42) * mm, "end": v(14, -2.42) * mm});
            skLineSegment(sketch, "E46.left", {"start": v(17, 47.58) * mm, "end": v(17, -0.42) * mm});
            skLineSegment(sketch, "E46.right", {"start": v(12, 47.58) * mm, "end": v(12, -0.42) * mm});
            skPoint(sketch, "E46.middle", {"position": v(14.5, 23.58) * mm});
            skLineSegment(sketch, "E47.bottom", {"start": v(0.5, -2.42) * mm, "end": v(-0.5, -2.42) * mm});
            skLineSegment(sketch, "E47.top", {"start": v(0.5, 49.58) * mm, "end": v(-0.5, 49.58) * mm});
            skLineSegment(sketch, "E47.left", {"start": v(2.5, -0.42) * mm, "end": v(2.5, 47.58) * mm});
            skLineSegment(sketch, "E47.right", {"start": v(-2.5, -0.42) * mm, "end": v(-2.5, 47.58) * mm});
            skPoint(sketch, "E47.middle", {"position": v(0, 23.58) * mm});
            skLineSegment(sketch, "E48.bottom", {"start": v(-14, -2.42) * mm, "end": v(-15, -2.42) * mm});
            skLineSegment(sketch, "E48.top", {"start": v(-14, 49.58) * mm, "end": v(-15, 49.58) * mm});
            skLineSegment(sketch, "E48.left", {"start": v(-12, -0.42) * mm, "end": v(-12, 47.58) * mm});
            skLineSegment(sketch, "E48.right", {"start": v(-17, -0.42) * mm, "end": v(-17, 47.58) * mm});
            skPoint(sketch, "E48.middle", {"position": v(-14.5, 23.58) * mm});
            skPoint(sketch, "E49.visualSharp", {"position": v(12, -2.42) * mm});
            skArc(sketch, "E49.filletArc", {"start": v(12, -0.42) * mm, "mid": v(12.59, -1.83) * mm, "end": v(14, -2.42) * mm});
            skPoint(sketch, "E50.visualSharp", {"position": v(17, -2.42) * mm});
            skArc(sketch, "E50.filletArc", {"start": v(15, -2.42) * mm, "mid": v(16.41, -1.83) * mm, "end": v(17, -0.42) * mm});
            skPoint(sketch, "E51.visualSharp", {"position": v(17, 49.58) * mm});
            skArc(sketch, "E51.filletArc", {"start": v(17, 47.58) * mm, "mid": v(16.41, 49) * mm, "end": v(15, 49.58) * mm});
            skPoint(sketch, "E52.visualSharp", {"position": v(12, 49.58) * mm});
            skArc(sketch, "E52.filletArc", {"start": v(14, 49.58) * mm, "mid": v(12.59, 49) * mm, "end": v(12, 47.58) * mm});
            skPoint(sketch, "E53.visualSharp", {"position": v(2.5, 49.58) * mm});
            skArc(sketch, "E53.filletArc", {"start": v(2.5, 47.58) * mm, "mid": v(1.91, 49) * mm, "end": v(0.5, 49.58) * mm});
            skPoint(sketch, "E54.visualSharp", {"position": v(-2.5, 49.58) * mm});
            skArc(sketch, "E54.filletArc", {"start": v(-0.5, 49.58) * mm, "mid": v(-1.91, 49) * mm, "end": v(-2.5, 47.58) * mm});
            skPoint(sketch, "E55.visualSharp", {"position": v(-12, 49.58) * mm});
            skArc(sketch, "E55.filletArc", {"start": v(-12, 47.58) * mm, "mid": v(-12.59, 49) * mm, "end": v(-14, 49.58) * mm});
            skPoint(sketch, "E56.visualSharp", {"position": v(-17, 49.58) * mm});
            skArc(sketch, "E56.filletArc", {"start": v(-15, 49.58) * mm, "mid": v(-16.41, 49) * mm, "end": v(-17, 47.58) * mm});
            skPoint(sketch, "E57.visualSharp", {"position": v(-17, -2.42) * mm});
            skArc(sketch, "E57.filletArc", {"start": v(-17, -0.42) * mm, "mid": v(-16.41, -1.83) * mm, "end": v(-15, -2.42) * mm});
            skPoint(sketch, "E58.visualSharp", {"position": v(-12, -2.42) * mm});
            skArc(sketch, "E58.filletArc", {"start": v(-14, -2.42) * mm, "mid": v(-12.59, -1.83) * mm, "end": v(-12, -0.42) * mm});
            skPoint(sketch, "E59.visualSharp", {"position": v(-2.5, -2.42) * mm});
            skArc(sketch, "E59.filletArc", {"start": v(-2.5, -0.42) * mm, "mid": v(-1.91, -1.83) * mm, "end": v(-0.5, -2.42) * mm});
            skPoint(sketch, "E60.visualSharp", {"position": v(2.5, -2.42) * mm});
            skArc(sketch, "E60.filletArc", {"start": v(0.5, -2.42) * mm, "mid": v(1.91, -1.83) * mm, "end": v(2.5, -0.42) * mm});
            skSolve(sketch);
        }
        {
            var Q0;
            Q0=makeQuery(id+"F27.imprint","IMPRINT",FACE,{"disambiguationData":[TD([[makeQuery(id+"F27.imprint","IMPRINT",EDGE,{"derivedFrom":sQuery(id+"F27.wireOp",EDGE,"E46.bottom")}),1.0]])]});
            var Q1;
            Q1=makeQuery(id+"F27.imprint","IMPRINT",FACE,{"disambiguationData":[TD([[makeQuery(id+"F27.imprint","IMPRINT",EDGE,{"derivedFrom":sQuery(id+"F27.wireOp",EDGE,"E47.bottom")}),-1.0]])]});
            var Q2;
            Q2=makeQuery(id+"F27.imprint","IMPRINT",FACE,{"disambiguationData":[TD([[makeQuery(id+"F27.imprint","IMPRINT",EDGE,{"derivedFrom":sQuery(id+"F27.wireOp",EDGE,"E48.bottom")}),-1.0]])]});
            extrude(context, id + "F28", {"entities" : qUnion([Q0, Q1, Q2]), "operationType" : NewBodyOperationType.ADD, "depth" : 1.5 * mm, "offsetDistance" : 25 * mm});
        }
        {
            var Q0;
            Q0=makeQuery(id+"F28.opExtrude","CAP_FACE",FACE,{"disambiguationData":[OSD([sQuery(id+"F27.wireOp",EDGE,"E46.bottom"),sQuery(id+"F27.wireOp",EDGE,"E46.top"),sQuery(id+"F27.wireOp",EDGE,"E46.left"),sQuery(id+"F27.wireOp",EDGE,"E46.right"),sQuery(id+"F27.wireOp",EDGE,"E49.filletArc"),sQuery(id+"F27.wireOp",EDGE,"E50.filletArc"),sQuery(id+"F27.wireOp",EDGE,"E51.filletArc"),sQuery(id+"F27.wireOp",EDGE,"E52.filletArc")])],"isStart":false});
            var Q1;
            Q1=makeQuery(id+"F28.opExtrude","CAP_FACE",FACE,{"disambiguationData":[OSD([sQuery(id+"F27.wireOp",EDGE,"E47.bottom"),sQuery(id+"F27.wireOp",EDGE,"E47.top"),sQuery(id+"F27.wireOp",EDGE,"E47.left"),sQuery(id+"F27.wireOp",EDGE,"E47.right"),sQuery(id+"F27.wireOp",EDGE,"E53.filletArc"),sQuery(id+"F27.wireOp",EDGE,"E54.filletArc"),sQuery(id+"F27.wireOp",EDGE,"E59.filletArc"),sQuery(id+"F27.wireOp",EDGE,"E60.filletArc")])],"isStart":false});
            var Q2;
            Q2=makeQuery(id+"F28.opExtrude","CAP_FACE",FACE,{"disambiguationData":[OSD([sQuery(id+"F27.wireOp",EDGE,"E48.bottom"),sQuery(id+"F27.wireOp",EDGE,"E48.top"),sQuery(id+"F27.wireOp",EDGE,"E48.left"),sQuery(id+"F27.wireOp",EDGE,"E48.right"),sQuery(id+"F27.wireOp",EDGE,"E55.filletArc"),sQuery(id+"F27.wireOp",EDGE,"E56.filletArc"),sQuery(id+"F27.wireOp",EDGE,"E57.filletArc"),sQuery(id+"F27.wireOp",EDGE,"E58.filletArc")])],"isStart":false});
            fillet(context, id + "F29", {"entities" : qUnion([Q0, Q1, Q2]), "radius" : 1 * mm, "tangentPropagation" : true, "rho" : 0.1, "crossSection" : FilletCrossSection.CONIC, "allowEdgeOverflow" : false});
        }
        {
            var Q0;
            Q0=makeQuery(id+"F12.opExtrude","CAP_EDGE",EDGE,{"disambiguationData":[OSD([sQuery(id+"F11.wireOp",EDGE,"E12.top")])],"isStart":true});
            var Q1;
            Q1=makeQuery(id+"F12.opExtrude","CAP_FACE",FACE,{"disambiguationData":[OSD([sQuery(id+"F11.wireOp",EDGE,"E12.bottom"),sQuery(id+"F11.wireOp",EDGE,"E12.top"),sQuery(id+"F11.wireOp",EDGE,"E12.left"),sQuery(id+"F11.wireOp",EDGE,"E12.right")])],"isStart":false});
            var Q2;
            Q2=makeQuery(id+"F12.boolean.opBoolean","MERGE",FACE,{"derivedFrom":[makeQuery(id+"F10.opExtrude","SWEPT_FACE",FACE,{"disambiguationData":[OSD([sQuery(id+"F9.wireOp",EDGE,"E11.top")])]}),makeQuery(id+"F12.opExtrude","SWEPT_FACE",FACE,{"disambiguationData":[OSD([sQuery(id+"F11.wireOp",EDGE,"E12.bottom")])]})]});
            fillet(context, id + "F30", {"entities" : qUnion([Q0, Q1, Q2]), "radius" : 0.5 * mm, "tangentPropagation" : true, "allowEdgeOverflow" : false});
        }
    });
